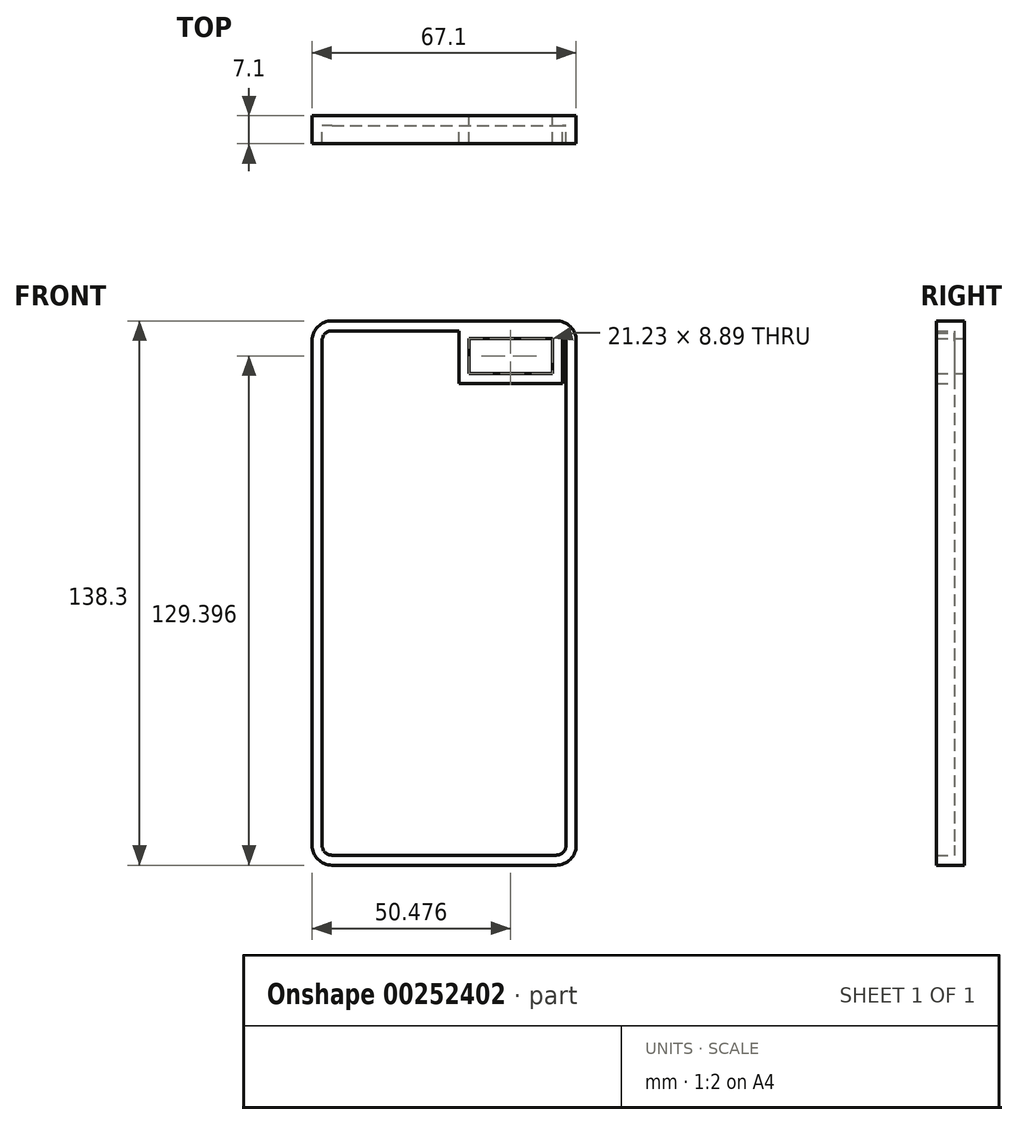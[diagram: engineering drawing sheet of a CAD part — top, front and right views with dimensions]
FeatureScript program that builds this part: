
annotation { "Feature Type Name" : "Feature", "Feature Type Description" : "" }
export const myFeature = defineFeature(function(context is Context, id is Id, definition is map)
    precondition{}
    {
        {
            var Q0;
            Q0=qCreatedBy(makeId("Front.planeOp"),FACE);
            var sketch = newSketch(context, id + "F0", { "sketchPlane" : qUnion([Q0])});
            skLineSegment(sketch, "E0.bottom", {"start": v(-33.55, 69.15) * mm, "end": v(33.55, 69.15) * mm});
            skLineSegment(sketch, "E0.top", {"start": v(-33.55, -69.15) * mm, "end": v(33.55, -69.15) * mm});
            skLineSegment(sketch, "E0.left", {"start": v(-33.55, 69.15) * mm, "end": v(-33.55, -69.15) * mm});
            skLineSegment(sketch, "E0.right", {"start": v(33.55, 69.15) * mm, "end": v(33.55, -69.15) * mm});
            skPoint(sketch, "E0.middle", {"position": v(0, 0) * mm});
            skLineSegment(sketch, "E1.bottom", {"start": v(25.25, 55.8) * mm, "end": v(25.25, 55.8) * mm});
            skLineSegment(sketch, "E1.top", {"start": v(25.25, 55.8) * mm, "end": v(25.25, 55.8) * mm});
            skLineSegment(sketch, "E1.left", {"start": v(25.25, 55.8) * mm, "end": v(25.25, 55.8) * mm});
            skLineSegment(sketch, "E1.right", {"start": v(25.25, 55.8) * mm, "end": v(25.25, 55.8) * mm});
            skLineSegment(sketch, "E2.bottom", {"start": v(6.31, 64.7) * mm, "end": v(27.54, 64.7) * mm});
            skLineSegment(sketch, "E2.top", {"start": v(6.31, 55.8) * mm, "end": v(27.54, 55.8) * mm});
            skLineSegment(sketch, "E2.left", {"start": v(6.31, 64.7) * mm, "end": v(6.31, 55.8) * mm});
            skLineSegment(sketch, "E2.right", {"start": v(27.54, 64.7) * mm, "end": v(27.54, 55.8) * mm});
            skSolve(sketch);
        }
        {
            var Q0;
            Q0=makeQuery(id+"F0.imprint","IMPRINT",FACE,{"disambiguationData":[TD([[makeQuery(id+"F0.imprint","IMPRINT",EDGE,{"derivedFrom":sQuery(id+"F0.wireOp",EDGE,"E0.bottom")}),-1.0]])]});
            extrude(context, id + "F1", {"entities" : qUnion([Q0]), "endBound" : BoundingType.SYMMETRIC, "depth" : 7.1 * mm});
        }
        {
            var Q0;
            Q0=makeQuery(id+"F1.opExtrude","SWEPT_EDGE",EDGE,{"disambiguationData":[OSD([sQuery(id+"F0.wireOp",EDGE,"E0.bottom"),sQuery(id+"F0.wireOp",EDGE,"E0.right")])]});
            var Q1;
            Q1=makeQuery(id+"F1.opExtrude","SWEPT_EDGE",EDGE,{"disambiguationData":[OSD([sQuery(id+"F0.wireOp",EDGE,"E0.bottom"),sQuery(id+"F0.wireOp",EDGE,"E0.left")])]});
            var Q2;
            Q2=makeQuery(id+"F1.opExtrude","SWEPT_EDGE",EDGE,{"disambiguationData":[OSD([sQuery(id+"F0.wireOp",EDGE,"E0.top"),sQuery(id+"F0.wireOp",EDGE,"E0.right")])]});
            var Q3;
            Q3=makeQuery(id+"F1.opExtrude","SWEPT_EDGE",EDGE,{"disambiguationData":[OSD([sQuery(id+"F0.wireOp",EDGE,"E0.top"),sQuery(id+"F0.wireOp",EDGE,"E0.left")])]});
            fillet(context, id + "F2", {"entities" : qUnion([Q0, Q1, Q2, Q3]), "radius" : 5.08 * mm, "tangentPropagation" : true, "allowEdgeOverflow" : false});
        }
        {
            var Q0;
            Q0=makeQuery(id+"F1.opExtrude","CAP_FACE",FACE,{"disambiguationData":[OSD([sQuery(id+"F0.wireOp",EDGE,"E0.bottom"),sQuery(id+"F0.wireOp",EDGE,"E0.top"),sQuery(id+"F0.wireOp",EDGE,"E0.left"),sQuery(id+"F0.wireOp",EDGE,"E0.right")])],"isStart":false});
            shell(context, id + "F3", {"entities" : qUnion([Q0]), "thickness" : 2.54 * mm});
        }
    });
